# Revit family: 63_UN_LF_Surface Mounted Titan XF 13_LI
name_source: partatom
category: Lighting Fixtures
units: mm (PartAtom-declared; Revit-internal decimal feet)

## family parameters
Always vertical = Yes
Cut with Voids When Loaded = Yes
Light Source = No
OmniClass Number = 23.80.70.11.14.11
OmniClass Title = Downlights
Part Type = Normal
Room Calculation Point = Yes
Round Connector Dimension = Use Diameter
Shared = No
Work Plane-Based = No

## types (1)
- Titan XF 13 - Wall mounted
    Apparent Load = 24 VA
    Assembly Code = 63.0
    Housing_Material = Plastic, Opaque Black
    IfcExportAs = IfcLightFixtureType
    IfcExportType = USERDEFINED
    Lamp = LED
    Light Source = XF13 Geometry : TXF13 Geometry
    Luminous Flux (lm) = 4320 lm
    Manufacturer = Light International
    Model = TITAN
    Type Comments = XF13
    URL = https://lightinternational.nl
    Voltage = 230 V
    Wattage Comments = 24W

## geometry (parser evidence)
native form markers: Sweep x16
no freeform markers — native parametric forms only
